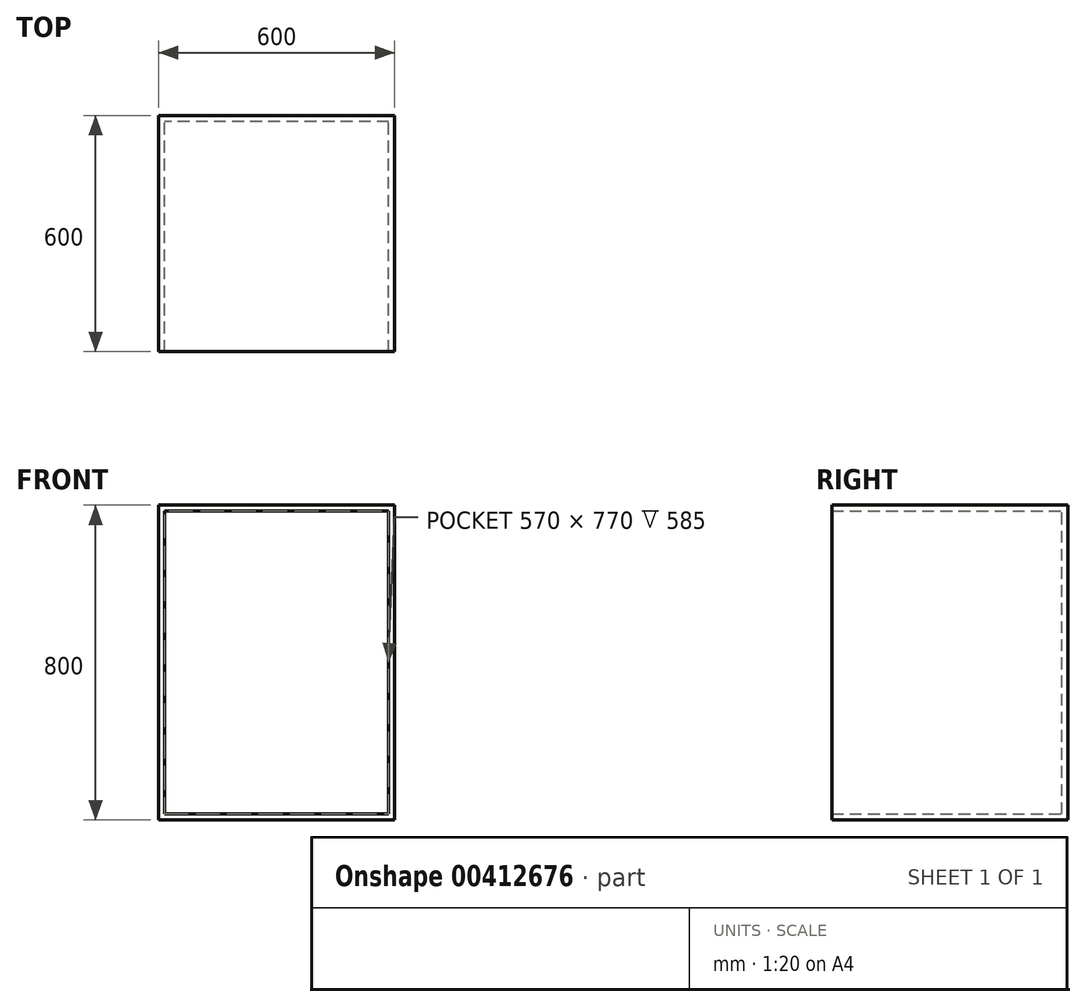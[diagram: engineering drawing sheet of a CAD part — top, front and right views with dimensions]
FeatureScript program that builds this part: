
annotation { "Feature Type Name" : "Feature", "Feature Type Description" : "" }
export const myFeature = defineFeature(function(context is Context, id is Id, definition is map)
    precondition{}
    {
        {
            var Q0;
            Q0=qCreatedBy(makeId("Right.planeOp"),FACE);
            var sketch = newSketch(context, id + "F0", { "sketchPlane" : qUnion([Q0])});
            skLineSegment(sketch, "E0.bottom", {"start": v(0, 0) * mm, "end": v(600, 0) * mm});
            skLineSegment(sketch, "E0.top", {"start": v(0, 800) * mm, "end": v(600, 800) * mm});
            skLineSegment(sketch, "E0.left", {"start": v(0, 0) * mm, "end": v(0, 800) * mm});
            skLineSegment(sketch, "E0.right", {"start": v(600, 0) * mm, "end": v(600, 800) * mm});
            skSolve(sketch);
        }
        {
            var Q0;
            Q0=makeQuery(id+"F0.imprint","IMPRINT",FACE,{"disambiguationData":[TD([[makeQuery(id+"F0.imprint","IMPRINT",EDGE,{"derivedFrom":sQuery(id+"F0.wireOp",EDGE,"E0.bottom")}),1.0]])]});
            extrude(context, id + "F1", {"entities" : qUnion([Q0]), "depth" : 600 * mm});
        }
        {
            var Q0;
            Q0=makeQuery(id+"F1.opExtrude","SWEPT_FACE",FACE,{"disambiguationData":[OSD([sQuery(id+"F0.wireOp",EDGE,"E0.left")])]});
            shell(context, id + "F2", {"entities" : qUnion([Q0]), "thickness" : 15 * mm});
        }
        {
            var Q0;
            Q0=makeQuery(id+"F1.opExtrude","SWEPT_BODY",BODY,{"disambiguationData":[OSD([sQuery(id+"F0.wireOp",EDGE,"E0.bottom"),sQuery(id+"F0.wireOp",EDGE,"E0.top"),sQuery(id+"F0.wireOp",EDGE,"E0.left"),sQuery(id+"F0.wireOp",EDGE,"E0.right")])]});
            transform(context, id + "F3", {"entities" : qUnion([Q0]), "transformType" : TransformType.TRANSLATION_3D, "dx" : 700 * mm, "dy" : 0 * mm, "dz" : 0 * mm, "makeCopy" : true});
        }
        {
            var Q0;
            Q0=makeQuery(id+"F3.opPattern","COPY",BODY,{"derivedFrom":makeQuery(id+"F1.opExtrude","SWEPT_BODY",BODY,{"disambiguationData":[OSD([sQuery(id+"F0.wireOp",EDGE,"E0.bottom"),sQuery(id+"F0.wireOp",EDGE,"E0.top"),sQuery(id+"F0.wireOp",EDGE,"E0.left"),sQuery(id+"F0.wireOp",EDGE,"E0.right")])]}),"instanceName":"1"});
            deleteBodies(context, id + "F4", {"entities" : qUnion([Q0])});
        }
    });
